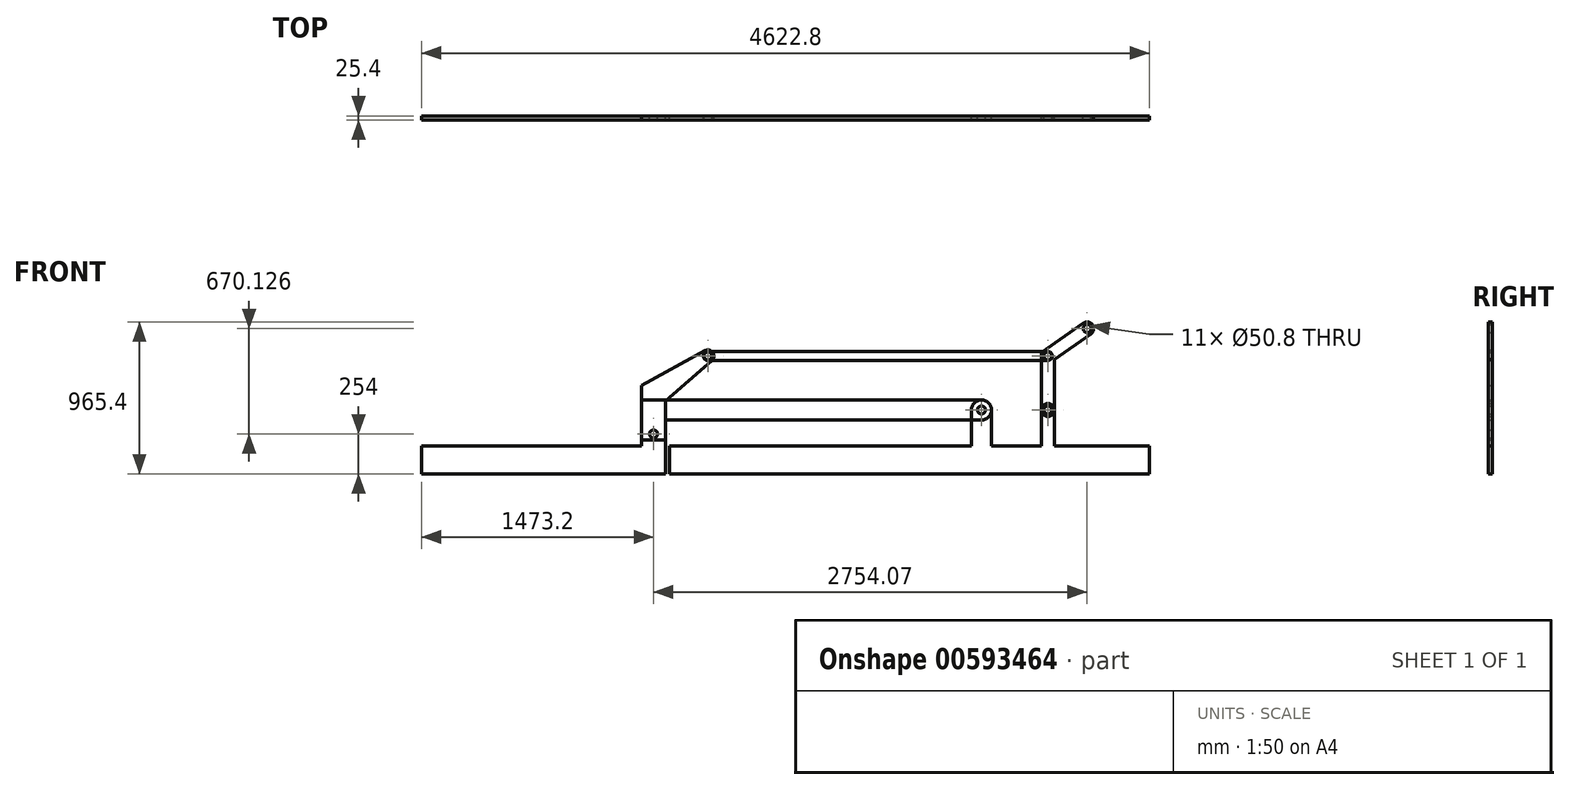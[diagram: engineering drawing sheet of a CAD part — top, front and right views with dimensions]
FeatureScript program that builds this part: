
annotation { "Feature Type Name" : "Feature", "Feature Type Description" : "" }
export const myFeature = defineFeature(function(context is Context, id is Id, definition is map)
    precondition{}
    {
        {
            var Q0;
            Q0=qCreatedBy(makeId("Front.planeOp"),FACE);
            var sketch = newSketch(context, id + "F0", { "sketchPlane" : qUnion([Q0])});
            skLineSegment(sketch, "E0", {"start": v(0, 0) * mm, "end": v(0, 342.9) * mm});
            skLineSegment(sketch, "E1", {"start": v(0, 342.9) * mm, "end": v(-2159, 342.9) * mm});
            skLineSegment(sketch, "E2", {"start": v(-2159, 342.9) * mm, "end": v(-2504.39, 101.06) * mm});
            skLineSegment(sketch, "E3", {"start": v(-2504.39, 101.06) * mm, "end": v(-2504.39, -152.4) * mm});
            skLineSegment(sketch, "E4", {"start": v(-421.59, 0) * mm, "end": v(-2504.39, 0) * mm});
            skLineSegment(sketch, "E5.bottom", {"start": v(-2453.59, -228.6) * mm, "end": v(-3977.59, -228.6) * mm});
            skLineSegment(sketch, "E5.top", {"start": v(-2453.59, -406.4) * mm, "end": v(-3977.59, -406.4) * mm});
            skLineSegment(sketch, "E5.left", {"start": v(-2453.59, -228.6) * mm, "end": v(-2453.59, -406.4) * mm});
            skLineSegment(sketch, "E5.right", {"start": v(-3977.59, -228.6) * mm, "end": v(-3977.59, -406.4) * mm});
            skLineSegment(sketch, "E6.bottom", {"start": v(-2402.79, -228.6) * mm, "end": v(645.21, -228.6) * mm});
            skLineSegment(sketch, "E6.top", {"start": v(-2402.79, -406.4) * mm, "end": v(645.21, -406.4) * mm});
            skLineSegment(sketch, "E6.left", {"start": v(-2402.79, -228.6) * mm, "end": v(-2402.79, -406.4) * mm});
            skLineSegment(sketch, "E6.right", {"start": v(645.21, -228.6) * mm, "end": v(645.21, -406.4) * mm});
            skLineSegment(sketch, "E7", {"start": v(0, 342.9) * mm, "end": v(249.68, 517.73) * mm});
            skSolve(sketch);
        }
        {
            var Q0;
            Q0=qCreatedBy(makeId("Front.planeOp"),FACE);
            var sketch = newSketch(context, id + "F1", { "sketchPlane" : qUnion([Q0])});
            skCircle(sketch, "E8", {"center": v(-2159, 342.9) * mm, "radius": 25.4 * mm});
            skCircle(sketch, "E9", {"center": v(-2504.39, -152.4) * mm, "radius": 25.4 * mm});
            skArc(sketch, "E10.0", {"start": v(-2133.9, 314.24) * mm, "mid": v(-2127.8, 364.75) * mm, "end": v(-2177.35, 376.3) * mm});
            skLineSegment(sketch, "E11", {"start": v(-2133.9, 314.24) * mm, "end": v(-2428.19, 56.52) * mm});
            skLineSegment(sketch, "E12", {"start": v(-2428.19, 56.52) * mm, "end": v(-2428.19, -406.4) * mm});
            skLineSegment(sketch, "E13", {"start": v(-2428.19, -406.4) * mm, "end": v(-2580.59, -406.4) * mm});
            skLineSegment(sketch, "E14", {"start": v(-2580.59, -406.4) * mm, "end": v(-2580.59, 154.7) * mm});
            skLineSegment(sketch, "E15", {"start": v(-2580.59, 154.7) * mm, "end": v(-2177.35, 376.3) * mm});
            skLineSegment(sketch, "E16", {"start": v(-2580.59, 154.7) * mm, "end": v(-2428.19, 56.52) * mm, "construction": true});
            skSolve(sketch);
        }
        {
            var Q0;
            Q0 = qSketchRegion(id + "F1", true);
            extrude(context, id + "F2", {"entities" : qUnion([Q0]), "depth" : 25.4 * mm, "offsetDistance" : 25.4 * mm});
        }
        {
            var Q0;
            Q0=qCreatedBy(makeId("Front.planeOp"),FACE);
            var sketch = newSketch(context, id + "F3", { "sketchPlane" : qUnion([Q0])});
            skCircle(sketch, "E17", {"center": v(-421.59, 0) * mm, "radius": 25.4 * mm});
            skCircle(sketch, "E18", {"center": v(-2504.39, -152.4) * mm, "radius": 25.4 * mm});
            skArc(sketch, "E19", {"start": v(-421.59, -63.5) * mm, "mid": v(-358.09, 0) * mm, "end": v(-421.59, 63.5) * mm});
            skLineSegment(sketch, "E20", {"start": v(-421.59, 63.5) * mm, "end": v(-2580.59, 63.5) * mm});
            skLineSegment(sketch, "E21", {"start": v(-2580.59, 63.5) * mm, "end": v(-2580.59, -190.5) * mm});
            skLineSegment(sketch, "E22", {"start": v(-2580.59, -190.5) * mm, "end": v(-2428.19, -190.5) * mm});
            skLineSegment(sketch, "E23", {"start": v(-2428.19, -190.5) * mm, "end": v(-2428.19, -63.5) * mm});
            skLineSegment(sketch, "E24", {"start": v(-2428.19, -63.5) * mm, "end": v(-421.59, -63.5) * mm});
            skSolve(sketch);
        }
        {
            var Q0;
            Q0 = qSketchRegion(id + "F3", true);
            extrude(context, id + "F4", {"entities" : qUnion([Q0]), "depth" : 25.4 * mm, "offsetDistance" : 25.4 * mm});
        }
        {
            var Q0;
            Q0=qCreatedBy(makeId("Front.planeOp"),FACE);
            var sketch = newSketch(context, id + "F5", { "sketchPlane" : qUnion([Q0])});
            skCircle(sketch, "E25", {"center": v(0, 0) * mm, "radius": 25.4 * mm});
            skCircle(sketch, "E26", {"center": v(0, 342.9) * mm, "radius": 25.4 * mm});
            skCircle(sketch, "E27", {"center": v(249.68, 517.73) * mm, "radius": 25.4 * mm});
            skArc(sketch, "E28", {"start": v(273.35, 483.92) * mm, "mid": v(283.49, 541.4) * mm, "end": v(226, 551.54) * mm});
            skArc(sketch, "E29", {"start": v(-41.28, 0) * mm, "mid": v(0, -41.28) * mm, "end": v(41.28, 0) * mm});
            skLineSegment(sketch, "E30", {"start": v(41.28, 0) * mm, "end": v(41.28, 321.41) * mm});
            skLineSegment(sketch, "E31", {"start": v(41.27, 321.41) * mm, "end": v(273.35, 483.92) * mm});
            skLineSegment(sketch, "E32", {"start": v(226, 551.54) * mm, "end": v(-41.28, 364.39) * mm});
            skLineSegment(sketch, "E33", {"start": v(-41.28, 364.39) * mm, "end": v(-41.28, 0) * mm});
            skLineSegment(sketch, "E34", {"start": v(41.27, 321.41) * mm, "end": v(-41.27, 364.39) * mm, "construction": true});
            skSolve(sketch);
        }
        {
            var Q0;
            Q0 = qSketchRegion(id + "F5", true);
            extrude(context, id + "F6", {"entities" : qUnion([Q0]), "depth" : 25.4 * mm, "offsetDistance" : 25.4 * mm});
        }
        {
            var Q0;
            Q0=qCreatedBy(makeId("Front.planeOp"),FACE);
            var sketch = newSketch(context, id + "F7", { "sketchPlane" : qUnion([Q0])});
            skCircle(sketch, "E35", {"center": v(-2159, 342.9) * mm, "radius": 25.4 * mm});
            skCircle(sketch, "E36", {"center": v(0, 342.9) * mm, "radius": 25.4 * mm});
            skArc(sketch, "E37", {"start": v(-2159, 371.47) * mm, "mid": v(-2187.58, 342.9) * mm, "end": v(-2159, 314.32) * mm});
            skArc(sketch, "E38", {"start": v(0, 314.33) * mm, "mid": v(28.58, 342.9) * mm, "end": v(0, 371.48) * mm});
            skLineSegment(sketch, "E39", {"start": v(-2159, 371.47) * mm, "end": v(0, 371.47) * mm});
            skLineSegment(sketch, "E40", {"start": v(0, 314.33) * mm, "end": v(-2159, 314.32) * mm});
            skSolve(sketch);
        }
        {
            var Q0;
            Q0 = qSketchRegion(id + "F7", true);
            extrude(context, id + "F8", {"entities" : qUnion([Q0]), "depth" : 25.4 * mm, "offsetDistance" : 25.4 * mm});
        }
        {
            var Q0;
            Q0=qCreatedBy(makeId("Front.planeOp"),FACE);
            var sketch = newSketch(context, id + "F9", { "sketchPlane" : qUnion([Q0])});
            skLineSegment(sketch, "E41.bottom", {"start": v(-2402.79, -228.6) * mm, "end": v(-485.09, -228.6) * mm});
            skLineSegment(sketch, "E41.top", {"start": v(-2402.79, -406.4) * mm, "end": v(645.21, -406.4) * mm});
            skLineSegment(sketch, "E41.left", {"start": v(-2402.79, -228.6) * mm, "end": v(-2402.79, -406.4) * mm});
            skLineSegment(sketch, "E41.right", {"start": v(645.21, -228.6) * mm, "end": v(645.21, -406.4) * mm});
            skCircle(sketch, "E42", {"center": v(-421.59, 0) * mm, "radius": 25.4 * mm});
            skCircle(sketch, "E43", {"center": v(0, 0) * mm, "radius": 25.4 * mm});
            skCircle(sketch, "E44", {"center": v(0, 0) * mm, "radius": 41.28 * mm});
            skCircle(sketch, "E45", {"center": v(-421.59, 0) * mm, "radius": 63.5 * mm});
            skLineSegment(sketch, "E46", {"start": v(-485.09, 0) * mm, "end": v(-485.09, -228.6) * mm});
            skLineSegment(sketch, "E47", {"start": v(-358.09, 0) * mm, "end": v(-358.09, -228.6) * mm});
            skLineSegment(sketch, "E48", {"start": v(-41.28, 0) * mm, "end": v(-41.27, -228.6) * mm});
            skLineSegment(sketch, "E49", {"start": v(41.28, 0) * mm, "end": v(41.28, -228.6) * mm});
            skLineSegment(sketch, "E50.trimOffspring", {"start": v(-358.09, -228.6) * mm, "end": v(-41.27, -228.6) * mm});
            skLineSegment(sketch, "E51.trimOffspring", {"start": v(41.28, -228.6) * mm, "end": v(645.21, -228.6) * mm});
            skSolve(sketch);
        }
        {
            var Q0;
            Q0 = qSketchRegion(id + "F9", true);
            extrude(context, id + "F10", {"entities" : qUnion([Q0]), "depth" : 25.4 * mm, "offsetDistance" : 25.4 * mm});
        }
        {
            var Q0;
            Q0=qCreatedBy(makeId("Front.planeOp"),FACE);
            var sketch = newSketch(context, id + "F11", { "sketchPlane" : qUnion([Q0])});
            skLineSegment(sketch, "E52.bottom", {"start": v(-3977.59, -228.6) * mm, "end": v(-2580.59, -228.6) * mm});
            skLineSegment(sketch, "E52.top", {"start": v(-3977.59, -406.4) * mm, "end": v(-2580.59, -406.4) * mm});
            skLineSegment(sketch, "E52.left", {"start": v(-3977.59, -228.6) * mm, "end": v(-3977.59, -406.4) * mm});
            skLineSegment(sketch, "E52.right", {"start": v(-2580.59, -228.6) * mm, "end": v(-2580.59, -406.4) * mm});
            skSolve(sketch);
        }
        {
            var Q0;
            Q0 = qSketchRegion(id + "F11", true);
            extrude(context, id + "F12", {"entities" : qUnion([Q0]), "operationType" : NewBodyOperationType.ADD, "depth" : 25.4 * mm, "offsetDistance" : 25.4 * mm});
        }
    });
